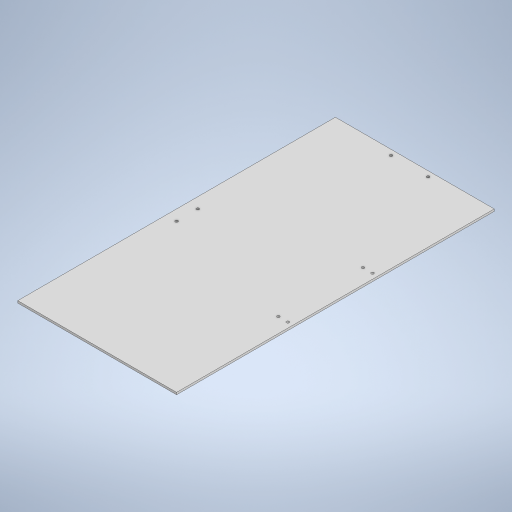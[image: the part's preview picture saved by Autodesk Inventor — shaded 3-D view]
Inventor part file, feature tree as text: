
AUTODESK INVENTOR PART (.ipt)
format: ipt  version: 2023 (Build 270158000, 158)  size: 255,488 bytes
history: native  units: mm
features: extrude x4, sketch x4, other x1
ambient origin geometry x8: Origin, YZ Plane, XZ Plane, XY Plane, X Axis, Y Axis, Z Axis, Center Point
bodies: Body1 (feature_tree)
feature tree (9):
  other  "Твердое тело1"
  extrude  "Выдавливание1"  Depth=300.0mm
  extrude  "Выдавливание2"  Depth=600.0mm
  extrude  "Выдавливание3"  Depth=4.0mm TaperAngle=0.0deg
  extrude  "Выдавливание4"  Depth=300.0mm
  sketch  "Эскиз1"
  sketch  "Эскиз2"
  sketch  "Эскиз3"
  sketch  "Эскиз4"
